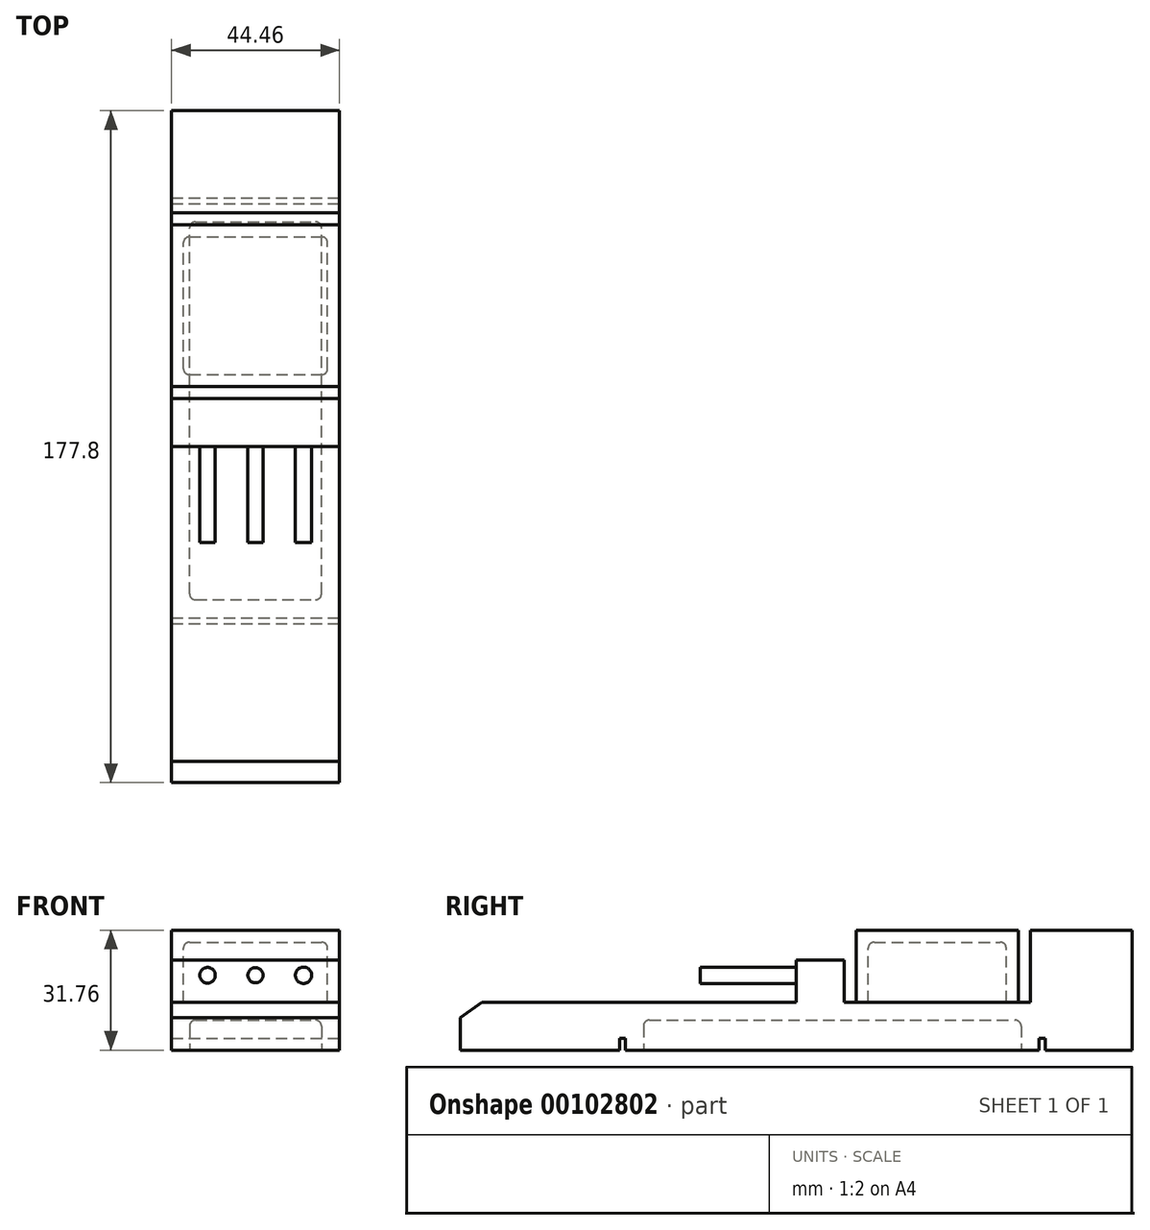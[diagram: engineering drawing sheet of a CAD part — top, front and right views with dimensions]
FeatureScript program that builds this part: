
annotation { "Feature Type Name" : "Feature", "Feature Type Description" : "" }
export const myFeature = defineFeature(function(context is Context, id is Id, definition is map)
    precondition{}
    {
        {
            var Q0;
            Q0=qCreatedBy(makeId("Right.planeOp"),FACE);
            var sketch = newSketch(context, id + "F0", { "sketchPlane" : qUnion([Q0])});
            skLineSegment(sketch, "E0.rect.bottom", {"start": v(-88.9, 15.88) * mm, "end": v(88.9, 15.88) * mm});
            skLineSegment(sketch, "E0.rect.top", {"start": v(-88.9, -15.88) * mm, "end": v(88.9, -15.88) * mm});
            skLineSegment(sketch, "E0.rect.left", {"start": v(-88.9, 15.88) * mm, "end": v(-88.9, -15.88) * mm});
            skLineSegment(sketch, "E0.rect.right", {"start": v(88.9, 15.88) * mm, "end": v(88.9, -15.88) * mm});
            skPoint(sketch, "E0.rect.middle", {"position": v(0, 0) * mm});
            skSolve(sketch);
        }
        {
            var Q0;
            Q0=makeQuery(id+"F0.imprint","IMPRINT",FACE,{"disambiguationData":[TD([[makeQuery(id+"F0.imprint","IMPRINT",EDGE,{"derivedFrom":sQuery(id+"F0.wireOp",EDGE,"E0.rect.bottom")}),-1.0]])]});
            extrude(context, id + "F1", {"entities" : qUnion([Q0]), "endBound" : BoundingType.SYMMETRIC, "depth" : 44.45 * mm});
        }
        {
            var Q0;
            Q0=qCreatedBy(makeId("Right.planeOp"),FACE);
            var sketch = newSketch(context, id + "F2", { "sketchPlane" : qUnion([Q0])});
            skLineSegment(sketch, "E1.bottom", {"start": v(-46.83, -15.88) * mm, "end": v(-45.24, -15.88) * mm});
            skLineSegment(sketch, "E1.top", {"start": v(-46.83, -12.7) * mm, "end": v(-45.24, -12.7) * mm});
            skLineSegment(sketch, "E1.left", {"start": v(-46.83, -15.87) * mm, "end": v(-46.83, -12.7) * mm});
            skLineSegment(sketch, "E1.right", {"start": v(-45.24, -15.87) * mm, "end": v(-45.24, -12.7) * mm});
            skLineSegment(sketch, "E2", {"start": v(-46.04, -12.7) * mm, "end": v(-46.04, -4.16) * mm, "construction": true});
            skLineSegment(sketch, "E3.bottom", {"start": v(64.3, -15.88) * mm, "end": v(65.88, -15.88) * mm});
            skLineSegment(sketch, "E3.top", {"start": v(64.3, -12.7) * mm, "end": v(65.88, -12.7) * mm});
            skLineSegment(sketch, "E3.left", {"start": v(64.3, -15.88) * mm, "end": v(64.3, -12.7) * mm});
            skLineSegment(sketch, "E3.right", {"start": v(65.88, -15.88) * mm, "end": v(65.88, -12.7) * mm});
            skCircle(sketch, "E4", {"center": v(-46.04, -13.7) * mm, "radius": 1 * mm, "construction": true});
            skCircle(sketch, "E5", {"center": v(65.09, -13.7) * mm, "radius": 1 * mm, "construction": true});
            skLineSegment(sketch, "E6", {"start": v(65.09, -13.7) * mm, "end": v(65.09, -12.7) * mm});
            skSolve(sketch);
        }
        {
            var Q0;
            {Q0=qUnion([makeQuery(id+"F2.imprint","IMPRINT",FACE,{"disambiguationData":[TD([[makeQuery(id+"F2.imprint","IMPRINT",EDGE,{"derivedFrom":sQuery(id+"F2.wireOp",EDGE,"E1.bottom")}),1.0]])]}),makeQuery(id+"F2.imprint","IMPRINT",FACE,{"disambiguationData":[TD([[makeQuery(id+"F2.imprint","IMPRINT",EDGE,{"derivedFrom":sQuery(id+"F2.wireOp",EDGE,"E3.bottom")}),1.0]])]})]);}
            extrude(context, id + "F3", {"entities" : qUnion([Q0]), "operationType" : NewBodyOperationType.REMOVE, "endBound" : BoundingType.SYMMETRIC, "oppositeDirection" : true, "depth" : 50.8 * mm});
        }
        {
            var Q0;
            Q0=qCreatedBy(makeId("Right.planeOp"),FACE);
            var sketch = newSketch(context, id + "F4", { "sketchPlane" : qUnion([Q0])});
            skLineSegment(sketch, "E7", {"start": v(-88.9, -7.34) * mm, "end": v(-83.2, -3.17) * mm});
            skLineSegment(sketch, "E8", {"start": v(-83.2, -3.17) * mm, "end": v(0, -3.17) * mm});
            skLineSegment(sketch, "E9", {"start": v(0, -3.17) * mm, "end": v(0, 7.94) * mm});
            skLineSegment(sketch, "E10", {"start": v(0, 7.94) * mm, "end": v(12.7, 7.94) * mm});
            skLineSegment(sketch, "E11", {"start": v(12.7, 7.94) * mm, "end": v(12.7, -3.17) * mm});
            skLineSegment(sketch, "E12", {"start": v(12.7, -3.17) * mm, "end": v(61.91, -3.17) * mm});
            skLineSegment(sketch, "E13", {"start": v(61.91, -3.17) * mm, "end": v(61.91, 15.88) * mm});
            skLineSegment(sketch, "E14", {"start": v(-88.9, -7.34) * mm, "end": v(-88.9, 15.88) * mm});
            skLineSegment(sketch, "E15", {"start": v(-88.9, 15.88) * mm, "end": v(61.91, 15.88) * mm});
            skSolve(sketch);
        }
        {
            var Q0;
            Q0 = qSketchRegion(id + "F4", true);
            var Q1;
            Q1=makeQuery(id+"F1.opExtrude","CAP_FACE",FACE,{"disambiguationData":[OSD([sQuery(id+"F0.wireOp",EDGE,"E0.rect.bottom"),sQuery(id+"F0.wireOp",EDGE,"E0.rect.top"),sQuery(id+"F0.wireOp",EDGE,"E0.rect.left"),sQuery(id+"F0.wireOp",EDGE,"E0.rect.right")])],"isStart":false});
            extrude(context, id + "F5", {"entities" : qUnion([Q0]), "operationType" : NewBodyOperationType.REMOVE, "endBound" : BoundingType.UP_TO_SURFACE, "endBoundEntityFace" : qUnion([Q1]), "depth" : 25.4 * mm, "hasSecondDirection" : true, "secondDirectionBound" : SecondDirectionBoundingType.THROUGH_ALL, "secondDirectionOppositeDirection" : true, "secondDirectionDepth" : 25.4 * mm});
        }
        {
            var Q0;
            Q0=qCreatedBy(makeId("Right.planeOp"),FACE);
            var sketch = newSketch(context, id + "F6", { "sketchPlane" : qUnion([Q0])});
            skLineSegment(sketch, "E16.bottom", {"start": v(58.74, -3.17) * mm, "end": v(15.88, -3.18) * mm});
            skLineSegment(sketch, "E16.top", {"start": v(58.74, 15.88) * mm, "end": v(15.87, 15.87) * mm});
            skLineSegment(sketch, "E16.left", {"start": v(58.74, -3.17) * mm, "end": v(58.74, 15.88) * mm});
            skLineSegment(sketch, "E16.right", {"start": v(15.88, -3.18) * mm, "end": v(15.87, 15.88) * mm});
            skSolve(sketch);
        }
        {
            var Q0;
            Q0 = qSketchRegion(id + "F6", true);
            var Q1;
            Q1=makeQuery(id+"F1.opExtrude","CAP_FACE",FACE,{"disambiguationData":[OSD([sQuery(id+"F0.wireOp",EDGE,"E0.rect.bottom"),sQuery(id+"F0.wireOp",EDGE,"E0.rect.top"),sQuery(id+"F0.wireOp",EDGE,"E0.rect.left"),sQuery(id+"F0.wireOp",EDGE,"E0.rect.right")])],"isStart":false});
            var Q2;
            Q2=makeQuery(id+"F1.opExtrude","CAP_FACE",FACE,{"disambiguationData":[OSD([sQuery(id+"F0.wireOp",EDGE,"E0.rect.bottom"),sQuery(id+"F0.wireOp",EDGE,"E0.rect.top"),sQuery(id+"F0.wireOp",EDGE,"E0.rect.left"),sQuery(id+"F0.wireOp",EDGE,"E0.rect.right")])],"isStart":true});
            extrude(context, id + "F7", {"entities" : qUnion([Q0]), "endBound" : BoundingType.UP_TO_SURFACE, "endBoundEntityFace" : qUnion([Q1]), "depth" : 25.4 * mm, "hasSecondDirection" : true, "secondDirectionBound" : SecondDirectionBoundingType.UP_TO_SURFACE, "secondDirectionOppositeDirection" : true, "secondDirectionBoundEntityFace" : qUnion([Q2]), "secondDirectionDepth" : 25.4 * mm});
        }
        {
            var Q0;
            Q0=makeQuery(id+"F5.boolean.opBoolean","COPY",FACE,{"derivedFrom":makeQuery(id+"F5.opExtrude","SWEPT_FACE",FACE,{"disambiguationData":[OSD([sQuery(id+"F4.wireOp",EDGE,"E9")])]})});
            var sketch = newSketch(context, id + "F8", { "sketchPlane" : qUnion([Q0])});
            skCircle(sketch, "E17", {"center": v(0, 3.93) * mm, "radius": 2.01 * mm});
            skCircle(sketch, "E18", {"center": v(-12.7, 3.93) * mm, "radius": 2.06 * mm});
            skCircle(sketch, "E19", {"center": v(12.7, 3.93) * mm, "radius": 2.17 * mm});
            skLineSegment(sketch, "E20", {"start": v(12.7, 3.93) * mm, "end": v(22.22, 3.93) * mm, "construction": true});
            skSolve(sketch);
        }
        {
            var Q0;
            Q0 = qSketchRegion(id + "F8", true);
            extrude(context, id + "F9", {"entities" : qUnion([Q0]), "operationType" : NewBodyOperationType.ADD, "depth" : 25.4 * mm});
        }
        {
            var Q0;
            {var subQ2=sQuery(id+"F0.wireOp",EDGE,"E0.rect.top");Q0=makeQuery(id+"F3.boolean.opBoolean","SPLIT",FACE,{"disambiguationData":[TD([makeQuery(id+"F3.opExtrude","SWEPT_FACE",FACE,{"disambiguationData":[OSD([sQuery(id+"F2.wireOp",EDGE,"E1.right")])]})])],"derivedFrom":makeQuery(id+"F1.opExtrude","SWEPT_FACE",FACE,{"disambiguationData":[OSD([subQ2])]})});}
            var sketch = newSketch(context, id + "F10", { "sketchPlane" : qUnion([Q0])});
            skLineSegment(sketch, "E21.bottom", {"start": v(-17.46, 40.48) * mm, "end": v(17.46, 40.48) * mm});
            skLineSegment(sketch, "E21.top", {"start": v(-17.46, -59.53) * mm, "end": v(17.46, -59.53) * mm});
            skLineSegment(sketch, "E21.left", {"start": v(-17.46, 40.48) * mm, "end": v(-17.46, -59.53) * mm});
            skLineSegment(sketch, "E21.right", {"start": v(17.46, 40.48) * mm, "end": v(17.46, -59.53) * mm});
            skSolve(sketch);
        }
        {
            var Q0;
            Q0 = qSketchRegion(id + "F10", true);
            extrude(context, id + "F11", {"entities" : qUnion([Q0]), "operationType" : NewBodyOperationType.REMOVE, "oppositeDirection" : true, "depth" : 7.94 * mm});
        }
        {
            var Q0;
            Q0=makeQuery(id+"F11.boolean.opBoolean","COPY",EDGE,{"derivedFrom":makeQuery(id+"F11.opExtrude","SWEPT_EDGE",EDGE,{"disambiguationData":[OSD([sQuery(id+"F10.wireOp",EDGE,"E21.bottom"),sQuery(id+"F10.wireOp",EDGE,"E21.right")])]})});
            var Q1;
            Q1=makeQuery(id+"F11.boolean.opBoolean","COPY",FACE,{"derivedFrom":makeQuery(id+"F11.opExtrude","CAP_FACE",FACE,{"disambiguationData":[OSD([sQuery(id+"F10.wireOp",EDGE,"E21.bottom"),sQuery(id+"F10.wireOp",EDGE,"E21.top"),sQuery(id+"F10.wireOp",EDGE,"E21.left"),sQuery(id+"F10.wireOp",EDGE,"E21.right")])],"isStart":false})});
            var Q2;
            Q2=makeQuery(id+"F11.boolean.opBoolean","COPY",EDGE,{"derivedFrom":makeQuery(id+"F11.opExtrude","SWEPT_EDGE",EDGE,{"disambiguationData":[OSD([sQuery(id+"F10.wireOp",EDGE,"E21.top"),sQuery(id+"F10.wireOp",EDGE,"E21.right")])]})});
            var Q3;
            Q3=makeQuery(id+"F11.boolean.opBoolean","COPY",EDGE,{"derivedFrom":makeQuery(id+"F11.opExtrude","SWEPT_EDGE",EDGE,{"disambiguationData":[OSD([sQuery(id+"F10.wireOp",EDGE,"E21.top"),sQuery(id+"F10.wireOp",EDGE,"E21.left")])]})});
            var Q4;
            Q4=makeQuery(id+"F11.boolean.opBoolean","COPY",EDGE,{"derivedFrom":makeQuery(id+"F11.opExtrude","SWEPT_EDGE",EDGE,{"disambiguationData":[OSD([sQuery(id+"F10.wireOp",EDGE,"E21.bottom"),sQuery(id+"F10.wireOp",EDGE,"E21.left")])]})});
            fillet(context, id + "F12", {"entities" : qUnion([Q0, Q1, Q2, Q3, Q4]), "radius" : 1.59 * mm, "tangentPropagation" : true, "allowEdgeOverflow" : false});
        }
        {
            var Q0;
            Q0=qCreatedBy(makeId("Right.planeOp"),FACE);
            var sketch = newSketch(context, id + "F13", { "sketchPlane" : qUnion([Q0])});
            skLineSegment(sketch, "E22.bottom", {"start": v(19.05, -3.17) * mm, "end": v(55.56, -3.17) * mm});
            skLineSegment(sketch, "E22.top", {"start": v(19.05, 12.7) * mm, "end": v(55.56, 12.7) * mm});
            skLineSegment(sketch, "E22.left", {"start": v(19.05, -3.17) * mm, "end": v(19.05, 12.7) * mm});
            skLineSegment(sketch, "E22.right", {"start": v(55.56, -3.17) * mm, "end": v(55.56, 12.7) * mm});
            skSolve(sketch);
        }
        {
            var Q0;
            Q0 = qSketchRegion(id + "F13", true);
            extrude(context, id + "F14", {"entities" : qUnion([Q0]), "operationType" : NewBodyOperationType.REMOVE, "endBound" : BoundingType.SYMMETRIC, "oppositeDirection" : true, "depth" : 38.1 * mm});
        }
        {
            var Q0;
            Q0=makeQuery(id+"F14.boolean.opBoolean","COPY",FACE,{"derivedFrom":makeQuery(id+"F14.opExtrude","SWEPT_FACE",FACE,{"disambiguationData":[OSD([sQuery(id+"F13.wireOp",EDGE,"E22.top")])]})});
            var Q1;
            Q1=makeQuery(id+"F14.boolean.opBoolean","COPY",EDGE,{"derivedFrom":makeQuery(id+"F14.opExtrude","CAP_EDGE",EDGE,{"disambiguationData":[OSD([sQuery(id+"F13.wireOp",EDGE,"E22.right")])],"isStart":true})});
            var Q2;
            Q2=makeQuery(id+"F14.boolean.opBoolean","COPY",EDGE,{"derivedFrom":makeQuery(id+"F14.opExtrude","CAP_EDGE",EDGE,{"disambiguationData":[OSD([sQuery(id+"F13.wireOp",EDGE,"E22.right")])],"isStart":false})});
            var Q3;
            Q3=makeQuery(id+"F14.boolean.opBoolean","COPY",EDGE,{"derivedFrom":makeQuery(id+"F14.opExtrude","CAP_EDGE",EDGE,{"disambiguationData":[OSD([sQuery(id+"F13.wireOp",EDGE,"E22.left")])],"isStart":false})});
            var Q4;
            Q4=makeQuery(id+"F14.boolean.opBoolean","COPY",EDGE,{"derivedFrom":makeQuery(id+"F14.opExtrude","CAP_EDGE",EDGE,{"disambiguationData":[OSD([sQuery(id+"F13.wireOp",EDGE,"E22.left")])],"isStart":true})});
            fillet(context, id + "F15", {"entities" : qUnion([Q0, Q1, Q2, Q3, Q4]), "radius" : 1.59 * mm, "tangentPropagation" : true, "allowEdgeOverflow" : false});
        }
    });
